# Revit family: Haworth_Epure_LShapeDesk_AP_PRELIMINARY
name_source: partatom
category: Furniture
units: mm (PartAtom-declared; Revit-internal decimal feet)

## family parameters
Always vertical = Yes
Cut with Voids When Loaded = No
OmniClass Number = 23.40.70.14.64.11
OmniClass Title = Office Furniture
Room Calculation Point = No
Shared = No
Work Plane-Based = No

## types (4) — shared parameters
Actual Height = 730 mm  [stored 2.39501 ft]
Assembly Code = E2020200
Cable Tray Finish = Haworth _ Polymer _ Undecided
Depth = 600 mm
Description = Haworth - Epure - L-Shape Desk
Flip Top Finish = Haworth _ Paint _ Metallic Silver
Leg Height = 695 mm  [stored 2.28018 ft]
Manufacturer = Haworth
Model = SYEPLS1X0X1X0XL
Revision Number = 1
Size = Verify Final Dim.w/ Haworth
Trim Finish = Haworth _ Metal _ Structured White EC
URL = https://www.haworth.com
URL - Product = https://www.haworth.com
Warranty = http://www.haworth.com
Worksurface Dimension = 1500/600 x 1500/600, 1600/600 x 1200/600, 1600/600 x 1600/600, 1800/600 x 1200/600 mm

## per-type parameters (varying)
| type | Accessory Kit | Actual Depth | Actual Width | Aluminium Legs | Cable Tray | Cable Tray Width | Flip Top Cable Outlet | No Accessory Kit | Round Cable Outlet | Umbilical Cord | Wooden Legs |
| 1500/600 x 1500/600 | No | 1500 mm  [stored 4.92126 ft] | 1500 mm  [stored 4.92126 ft] | Yes | No | 1000 mm | No | Yes | No | No | No |
| 1600/600 x 1600/600 | Yes | 1600 mm | 1600 mm | Yes | Yes | 1100 mm | No | No | Yes | Yes | No |
| 1800/600 x 1200/600 | Yes | 1200 mm | 1800 mm  [stored 5.90551 ft] | No | Yes | 1300 mm | No | No | No | Yes | Yes |
| 1600/600 x 1200/600 | Yes | 1200 mm | 1600 mm | No | Yes | 1100 mm | Yes | No | No | Yes | Yes |

type visibility flags: 4 boolean params named "<type name>" — each type sets only its own to Yes (folded from table)

note: [stored X ft] marks values corroborated as IEEE doubles in the binary element streams (Revit-internal decimal feet)

## geometry (parser evidence)
native form markers: Sweep x21
no freeform markers — native parametric forms only
